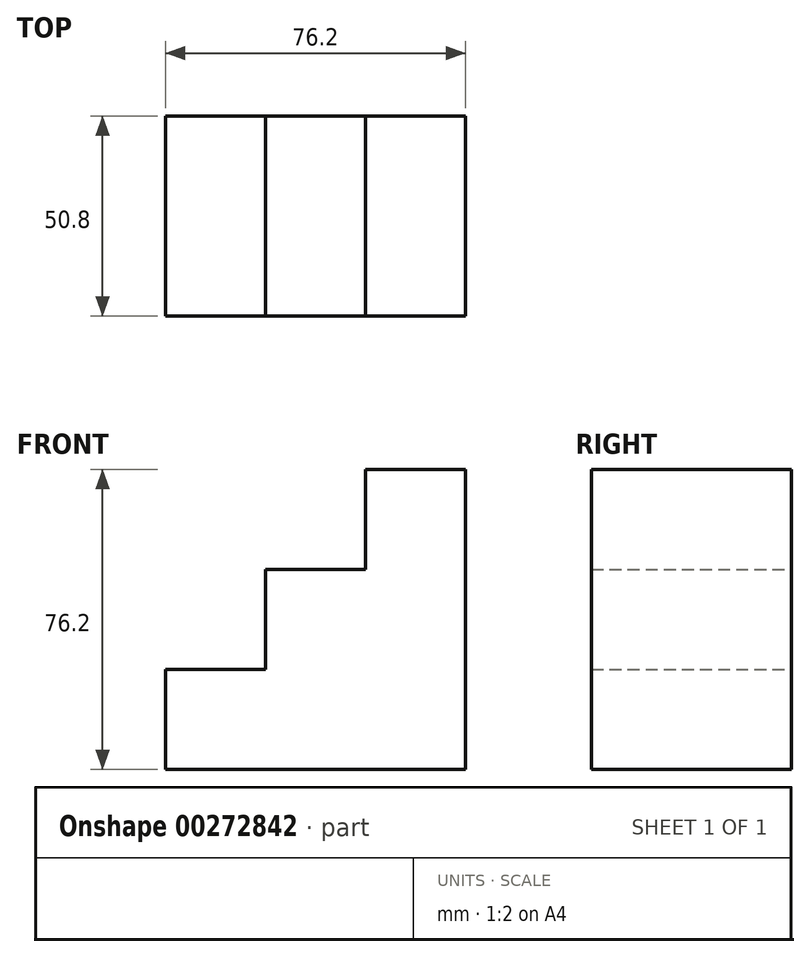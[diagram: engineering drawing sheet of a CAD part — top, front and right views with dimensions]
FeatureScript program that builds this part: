
annotation { "Feature Type Name" : "Feature", "Feature Type Description" : "" }
export const myFeature = defineFeature(function(context is Context, id is Id, definition is map)
    precondition{}
    {
        {
            var Q0;
            Q0=qCreatedBy(makeId("Front.planeOp"),FACE);
            var sketch = newSketch(context, id + "F0", { "sketchPlane" : qUnion([Q0])});
            skLineSegment(sketch, "E0", {"start": v(0, 0) * mm, "end": v(-76.2, 0) * mm});
            skLineSegment(sketch, "E1", {"start": v(0, 0) * mm, "end": v(0, 76.2) * mm});
            skLineSegment(sketch, "E2", {"start": v(0, 76.2) * mm, "end": v(-25.4, 76.2) * mm});
            skLineSegment(sketch, "E3", {"start": v(-25.4, 76.2) * mm, "end": v(-25.4, 50.8) * mm});
            skLineSegment(sketch, "E4", {"start": v(-25.4, 50.8) * mm, "end": v(-50.8, 50.8) * mm});
            skLineSegment(sketch, "E5", {"start": v(-50.8, 50.8) * mm, "end": v(-50.8, 25.4) * mm});
            skLineSegment(sketch, "E6", {"start": v(-50.8, 25.4) * mm, "end": v(-76.2, 25.4) * mm});
            skLineSegment(sketch, "E7", {"start": v(-76.2, 25.4) * mm, "end": v(-76.2, 0) * mm});
            skSolve(sketch);
        }
        {
            var Q0;
            Q0=makeQuery(id+"F0.imprint","IMPRINT",FACE,{"disambiguationData":[TD([[makeQuery(id+"F0.imprint","IMPRINT",EDGE,{"derivedFrom":sQuery(id+"F0.wireOp",EDGE,"E0")}),-1.0]])]});
            extrude(context, id + "F1", {"entities" : qUnion([Q0]), "depth" : 50.8 * mm});
        }
    });
